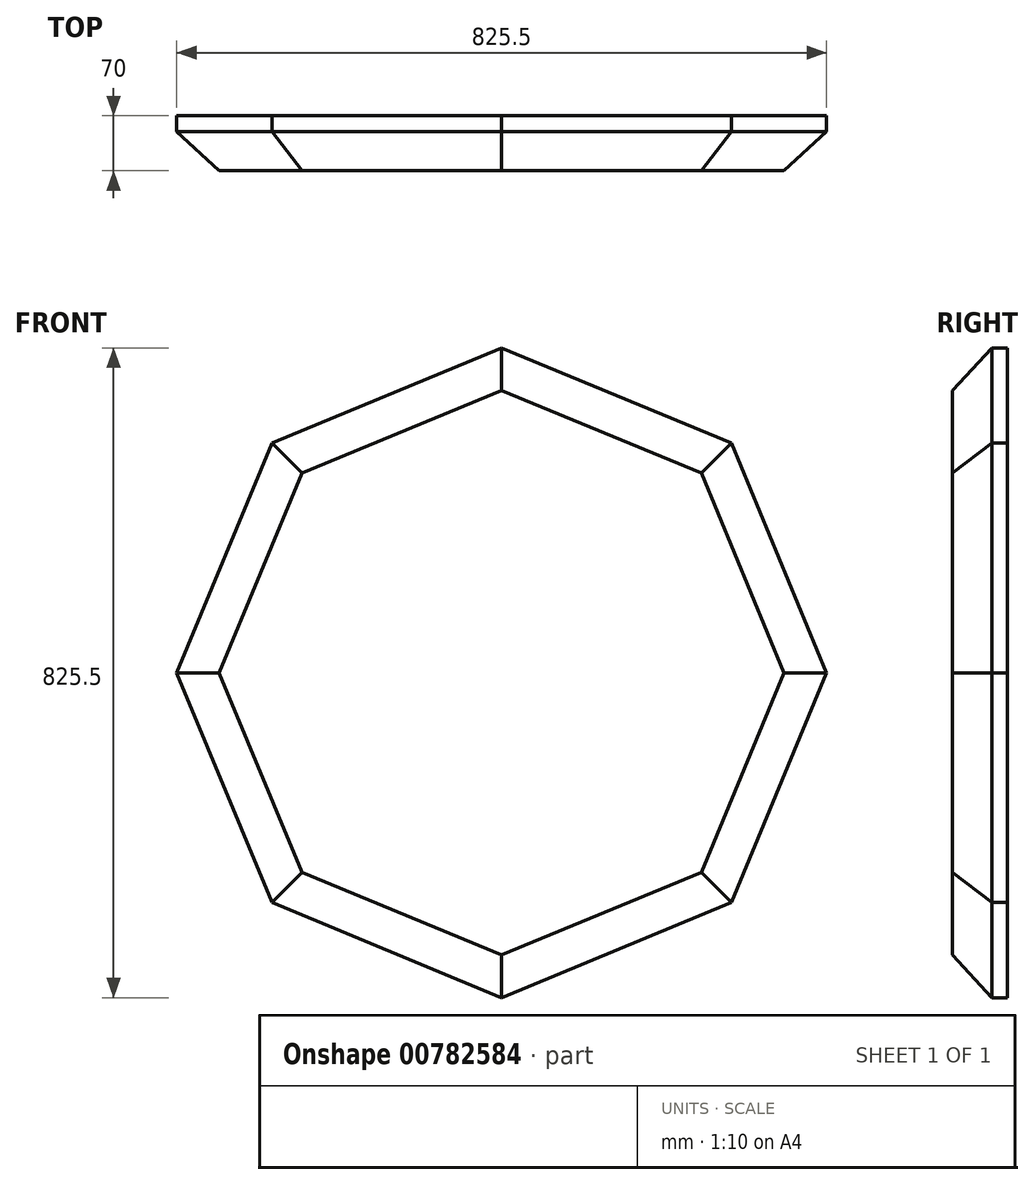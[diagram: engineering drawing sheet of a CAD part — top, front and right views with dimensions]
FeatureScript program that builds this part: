
annotation { "Feature Type Name" : "Feature", "Feature Type Description" : "" }
export const myFeature = defineFeature(function(context is Context, id is Id, definition is map)
    precondition{}
    {
        {
            var Q0;
            Q0=qCreatedBy(makeId("Front.planeOp"),FACE);
            var sketch = newSketch(context, id + "F0", { "sketchPlane" : qUnion([Q0])});
            skCircle(sketch, "E0.cCircle", {"center": v(0, 0) * mm, "radius": 412.75 * mm, "construction": true});
            skLineSegment(sketch, "E0.0", {"start": v(412.75, 0) * mm, "end": v(291.86, -291.86) * mm});
            skLineSegment(sketch, "E0.1", {"start": v(291.86, -291.86) * mm, "end": v(0, -412.75) * mm});
            skLineSegment(sketch, "E0.2", {"start": v(0, -412.75) * mm, "end": v(-291.86, -291.86) * mm});
            skLineSegment(sketch, "E0.3", {"start": v(-291.86, -291.86) * mm, "end": v(-412.75, 0) * mm});
            skLineSegment(sketch, "E0.4", {"start": v(-412.75, 0) * mm, "end": v(-291.86, 291.86) * mm});
            skLineSegment(sketch, "E0.5", {"start": v(-291.86, 291.86) * mm, "end": v(0, 412.75) * mm});
            skLineSegment(sketch, "E0.6", {"start": v(0, 412.75) * mm, "end": v(291.86, 291.86) * mm});
            skLineSegment(sketch, "E0.7", {"start": v(291.86, 291.86) * mm, "end": v(412.75, 0) * mm});
            skSolve(sketch);
        }
        {
            var Q0;
            Q0=makeQuery(id+"F0.imprint","IMPRINT",FACE,{"disambiguationData":[TD([[makeQuery(id+"F0.imprint","IMPRINT",EDGE,{"derivedFrom":sQuery(id+"F0.wireOp",EDGE,"E0.0")}),-1.0]])]});
            extrude(context, id + "F1", {"entities" : qUnion([Q0]), "depth" : 50 * mm, "offsetDistance" : 25 * mm});
        }
        {
            var Q0;
            Q0=makeQuery(id+"F1.opExtrude","CAP_EDGE",EDGE,{"disambiguationData":[OSD([sQuery(id+"F0.wireOp",EDGE,"E0.3")])],"isStart":false});
            var Q1;
            Q1=makeQuery(id+"F1.opExtrude","CAP_EDGE",EDGE,{"disambiguationData":[OSD([sQuery(id+"F0.wireOp",EDGE,"E0.2")])],"isStart":false});
            var Q2;
            Q2=makeQuery(id+"F1.opExtrude","CAP_EDGE",EDGE,{"disambiguationData":[OSD([sQuery(id+"F0.wireOp",EDGE,"E0.1")])],"isStart":false});
            var Q3;
            Q3=makeQuery(id+"F1.opExtrude","CAP_EDGE",EDGE,{"disambiguationData":[OSD([sQuery(id+"F0.wireOp",EDGE,"E0.0")])],"isStart":false});
            var Q4;
            Q4=makeQuery(id+"F1.opExtrude","CAP_EDGE",EDGE,{"disambiguationData":[OSD([sQuery(id+"F0.wireOp",EDGE,"E0.7")])],"isStart":false});
            var Q5;
            Q5=makeQuery(id+"F1.opExtrude","CAP_EDGE",EDGE,{"disambiguationData":[OSD([sQuery(id+"F0.wireOp",EDGE,"E0.6")])],"isStart":false});
            var Q6;
            Q6=makeQuery(id+"F1.opExtrude","CAP_FACE",FACE,{"disambiguationData":[OSD([sQuery(id+"F0.wireOp",EDGE,"E0.0"),sQuery(id+"F0.wireOp",EDGE,"E0.1"),sQuery(id+"F0.wireOp",EDGE,"E0.2"),sQuery(id+"F0.wireOp",EDGE,"E0.3"),sQuery(id+"F0.wireOp",EDGE,"E0.4"),sQuery(id+"F0.wireOp",EDGE,"E0.5"),sQuery(id+"F0.wireOp",EDGE,"E0.6"),sQuery(id+"F0.wireOp",EDGE,"E0.7")])],"isStart":false});
            var Q7;
            Q7=makeQuery(id+"F1.opExtrude","CAP_EDGE",EDGE,{"disambiguationData":[OSD([sQuery(id+"F0.wireOp",EDGE,"E0.5")])],"isStart":false});
            var Q8;
            Q8=makeQuery(id+"F1.opExtrude","CAP_EDGE",EDGE,{"disambiguationData":[OSD([sQuery(id+"F0.wireOp",EDGE,"E0.4")])],"isStart":false});
            chamfer(context, id + "F2", {"entities" : qUnion([Q0, Q1, Q2, Q3, Q4, Q5, Q6, Q7, Q8]), "width" : 50 * mm, "tangentPropagation" : true});
        }
        {
            var Q0;
            Q0=makeQuery(id+"F0.imprint","IMPRINT",FACE,{"disambiguationData":[TD([[makeQuery(id+"F0.imprint","IMPRINT",EDGE,{"derivedFrom":sQuery(id+"F0.wireOp",EDGE,"E0.0")}),-1.0]])]});
            extrude(context, id + "F3", {"entities" : qUnion([Q0]), "operationType" : NewBodyOperationType.ADD, "oppositeDirection" : true, "depth" : 20 * mm, "offsetDistance" : 25 * mm});
        }
    });
